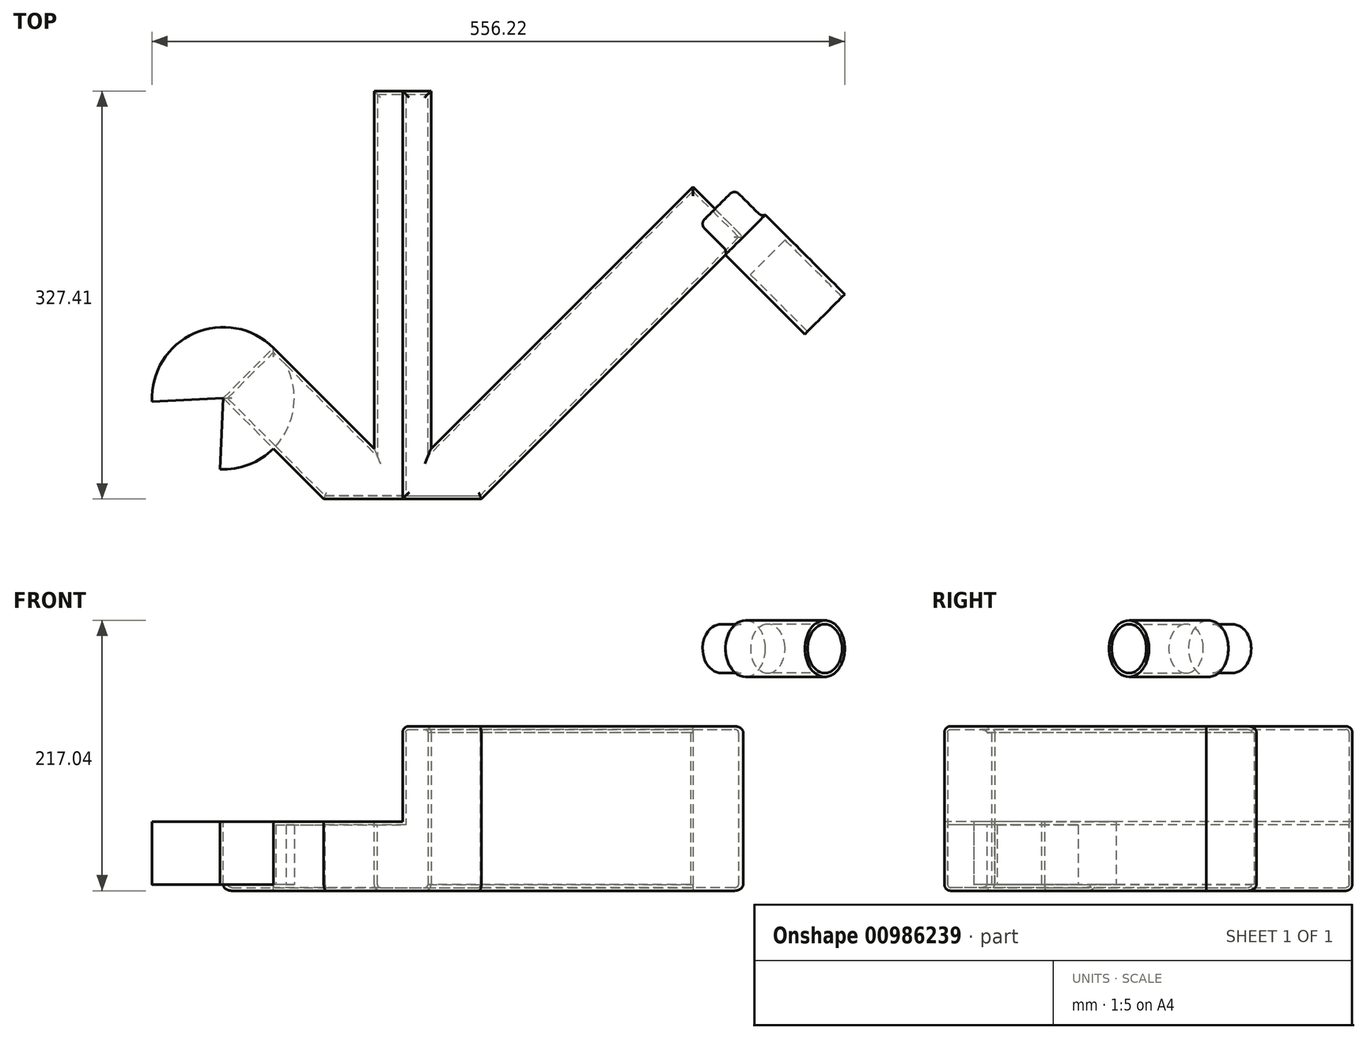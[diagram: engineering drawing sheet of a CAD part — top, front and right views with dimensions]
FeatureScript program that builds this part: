
annotation { "Feature Type Name" : "Feature", "Feature Type Description" : "" }
export const myFeature = defineFeature(function(context is Context, id is Id, definition is map)
    precondition{}
    {
        {
            var Q0;
            Q0=qCreatedBy(makeId("Top.planeOp"),FACE);
            var sketch = newSketch(context, id + "F0", { "sketchPlane" : qUnion([Q0])});
            skLineSegment(sketch, "E0", {"start": v(0, 0) * mm, "end": v(40.39, 40.39) * mm});
            skLineSegment(sketch, "E1", {"start": v(40.39, 40.39) * mm, "end": v(86.15, 40.39) * mm});
            skLineSegment(sketch, "E2", {"start": v(86.15, 40.39) * mm, "end": v(126.53, 0) * mm});
            skLineSegment(sketch, "E3", {"start": v(126.53, 0) * mm, "end": v(0, 0) * mm});
            skLineSegment(sketch, "E4", {"start": v(63.27, 40.39) * mm, "end": v(63.27, 0) * mm});
            skSolve(sketch);
        }
        {
            var Q0;
            {var subQ0=sQuery(id+"F0.wireOp",EDGE,"E2");Q0=makeQuery(id+"F0.imprint","IMPRINT",FACE,{"disambiguationData":[TD([[makeQuery(id+"F0.imprint","IMPRINT",EDGE,{"derivedFrom":subQ0}),-1.0]])]});}
            extrude(context, id + "F1", {"entities" : qUnion([Q0]), "depth" : 76.7 * mm, "offsetDistance" : 25.4 * mm});
        }
        {
            var Q0;
            Q0 = qSketchRegion(id + "F0", true);
            extrude(context, id + "F2", {"entities" : qUnion([Q0]), "operationType" : NewBodyOperationType.ADD, "oppositeDirection" : true, "depth" : 55.37 * mm, "offsetDistance" : 25.4 * mm});
        }
        {
            var Q0;
            {var subQ0=sQuery(id+"F0.wireOp",EDGE,"E1");Q0=makeQuery(id+"F2.boolean.opBoolean","MERGE",FACE,{"derivedFrom":[makeQuery(id+"F1.opExtrude","SWEPT_FACE",FACE,{"disambiguationData":[OSD([subQ0])]}),makeQuery(id+"F2.opExtrude","SWEPT_FACE",FACE,{"disambiguationData":[OSD([subQ0])]})]});}
            extrude(context, id + "F3", {"entities" : qUnion([Q0]), "operationType" : NewBodyOperationType.ADD, "depth" : 287.02 * mm, "offsetDistance" : 25.4 * mm});
        }
        {
            var Q0;
            {var subQ0=sQuery(id+"F0.wireOp",EDGE,"E2");Q0=makeQuery(id+"F2.boolean.opBoolean","MERGE",FACE,{"derivedFrom":[makeQuery(id+"F1.opExtrude","SWEPT_FACE",FACE,{"disambiguationData":[OSD([subQ0])]}),makeQuery(id+"F2.opExtrude","SWEPT_FACE",FACE,{"disambiguationData":[OSD([subQ0])]})]});}
            extrude(context, id + "F4", {"entities" : qUnion([Q0]), "operationType" : NewBodyOperationType.ADD, "depth" : 297.18 * mm, "offsetDistance" : 25.4 * mm});
        }
        {
            var Q0;
            Q0=makeQuery(id+"F2.opExtrude","SWEPT_FACE",FACE,{"disambiguationData":[OSD([sQuery(id+"F0.wireOp",EDGE,"E0")])]});
            extrude(context, id + "F5", {"entities" : qUnion([Q0]), "operationType" : NewBodyOperationType.ADD, "depth" : 114.3 * mm, "offsetDistance" : 25.4 * mm});
        }
        {
            var Q0;
            Q0=makeQuery(id+"F4.opExtrude","SWEPT_FACE",FACE,{"disambiguationData":[OSD([sQuery(id+"F0.wireOp",EDGE,"E2"),sQuery(id+"F0.wireOp",EDGE,"E3")])]});
            var sketch = newSketch(context, id + "F6", { "sketchPlane" : qUnion([Q0])});
            skCircle(sketch, "E5", {"center": v(389.23, 139) * mm, "radius": 22.67 * mm});
            skCircle(sketch, "E6", {"center": v(389.23, 139) * mm, "radius": 19.58 * mm});
            skSolve(sketch);
        }
        {
            var Q0;
            Q0 = qSketchRegion(id + "F6", true);
            var Q1;
            Q1=makeQuery(id+"F6.imprint","IMPRINT",FACE,{"disambiguationData":[TD([[makeQuery(id+"F6.imprint","IMPRINT",EDGE,{"derivedFrom":sQuery(id+"F6.wireOp",EDGE,"E5")}),1.0]])]});
            extrude(context, id + "F7", {"entities" : qUnion([Q0, Q1]), "depth" : 90.17 * mm, "offsetDistance" : 25.4 * mm});
        }
        {
            var Q0;
            Q0=makeQuery(id+"F6.imprint","IMPRINT",FACE,{"disambiguationData":[TD([[makeQuery(id+"F6.imprint","IMPRINT",EDGE,{"derivedFrom":sQuery(id+"F6.wireOp",EDGE,"E6")}),1.0]])]});
            extrude(context, id + "F8", {"entities" : qUnion([Q0]), "operationType" : NewBodyOperationType.ADD, "depth" : 25.4 * mm, "offsetDistance" : 25.4 * mm});
        }
        {
            var Q0;
            Q0=makeQuery(id+"F6.imprint","IMPRINT",FACE,{"disambiguationData":[TD([[makeQuery(id+"F6.imprint","IMPRINT",EDGE,{"derivedFrom":sQuery(id+"F6.wireOp",EDGE,"E6")}),1.0]])]});
            extrude(context, id + "F9", {"entities" : qUnion([Q0]), "operationType" : NewBodyOperationType.ADD, "oppositeDirection" : true, "depth" : 32 * mm, "offsetDistance" : 25.4 * mm});
        }
        {
            var Q0;
            {var subQ0=sQuery(id+"F0.wireOp",EDGE,"E2");var subQ1=sQuery(id+"F0.wireOp",EDGE,"E1");Q0=makeQuery(id+"F4.boolean.opBoolean","MERGE",FACE,{"derivedFrom":[makeQuery(id+"F3.boolean.opBoolean","MERGE",FACE,{"derivedFrom":[makeQuery(id+"F1.opExtrude","CAP_FACE",FACE,{"disambiguationData":[OSD([subQ1,subQ0,sQuery(id+"F0.wireOp",EDGE,"E3"),sQuery(id+"F0.wireOp",EDGE,"E4")])],"isStart":false}),makeQuery(id+"F3.opExtrude","SWEPT_FACE",FACE,{"disambiguationData":[OSD([subQ1]),TDD([makeQuery(id+"F1.opExtrude","CAP_EDGE",EDGE,{"disambiguationData":[OSD([subQ1])],"isStart":false})])]})]}),makeQuery(id+"F4.opExtrude","SWEPT_FACE",FACE,{"disambiguationData":[OSD([subQ0]),TDD([makeQuery(id+"F1.opExtrude","CAP_EDGE",EDGE,{"disambiguationData":[OSD([subQ0])],"isStart":false})])]})]});}
            fillet(context, id + "F10", {"entities" : qUnion([Q0]), "radius" : 5.08 * mm, "tangentPropagation" : true, "allowEdgeOverflow" : false});
        }
        {
            var Q0;
            {var subQ0=sQuery(id+"F0.wireOp",EDGE,"E0");var subQ1=sQuery(id+"F0.wireOp",EDGE,"E2");var subQ2=sQuery(id+"F0.wireOp",EDGE,"E1");Q0=makeQuery(id+"F5.boolean.opBoolean","MERGE",FACE,{"derivedFrom":[makeQuery(id+"F4.boolean.opBoolean","MERGE",FACE,{"derivedFrom":[makeQuery(id+"F3.boolean.opBoolean","MERGE",FACE,{"derivedFrom":[makeQuery(id+"F2.opExtrude","CAP_FACE",FACE,{"disambiguationData":[OSD([subQ0,subQ2,subQ1,sQuery(id+"F0.wireOp",EDGE,"E3")])],"isStart":false}),makeQuery(id+"F3.opExtrude","SWEPT_FACE",FACE,{"disambiguationData":[OSD([subQ2]),TDD([makeQuery(id+"F2.opExtrude","CAP_EDGE",EDGE,{"disambiguationData":[OSD([subQ2])],"isStart":false})])]})]}),makeQuery(id+"F4.opExtrude","SWEPT_FACE",FACE,{"disambiguationData":[OSD([subQ1]),TDD([makeQuery(id+"F2.opExtrude","CAP_EDGE",EDGE,{"disambiguationData":[OSD([subQ1])],"isStart":false})])]})]}),makeQuery(id+"F5.opExtrude","SWEPT_FACE",FACE,{"disambiguationData":[OSD([subQ0]),TDD([makeQuery(id+"F2.opExtrude","CAP_EDGE",EDGE,{"disambiguationData":[OSD([subQ0])],"isStart":false})])]})]});}
            fillet(context, id + "F11", {"entities" : qUnion([Q0]), "radius" : 5.08 * mm, "tangentPropagation" : true, "allowEdgeOverflow" : false});
        }
        {
            var Q0;
            Q0=makeQuery(id+"F9.opExtrude","SWEPT_FACE",FACE,{"disambiguationData":[OSD([sQuery(id+"F6.wireOp",EDGE,"E6")])]});
            fillet(context, id + "F12", {"entities" : qUnion([Q0]), "radius" : 5.08 * mm, "tangentPropagation" : true, "allowEdgeOverflow" : false});
        }
        {
            var Q0;
            Q0=makeQuery(id+"F4.opExtrude","SWEPT_FACE",FACE,{"disambiguationData":[OSD([sQuery(id+"F0.wireOp",EDGE,"E1"),sQuery(id+"F0.wireOp",EDGE,"E2")])]});
            shell(context, id + "F13", {"entities" : qUnion([Q0]), "thickness" : 2.54 * mm});
        }
        {
            var Q0;
            Q0=makeQuery(id+"F5.opExtrude","CAP_FACE",FACE,{"disambiguationData":[OSD([sQuery(id+"F0.wireOp",EDGE,"E0")])],"isStart":false});
            var Q1;
            Q1=makeQuery(id+"F5.opExtrude","CAP_EDGE",EDGE,{"disambiguationData":[OSD([sQuery(id+"F0.wireOp",EDGE,"E0"),sQuery(id+"F0.wireOp",EDGE,"E3")])],"isStart":false});
            revolve(context, id + "F14", {"operationType" : NewBodyOperationType.ADD, "surfaceOperationType" : NewSurfaceOperationType.NEW, "entities" : qUnion([Q0]), "axis" : qUnion([Q1]), "revolveType" : RevolveType.SYMMETRIC, "angle" : 275.3 * degree});
        }
    });
